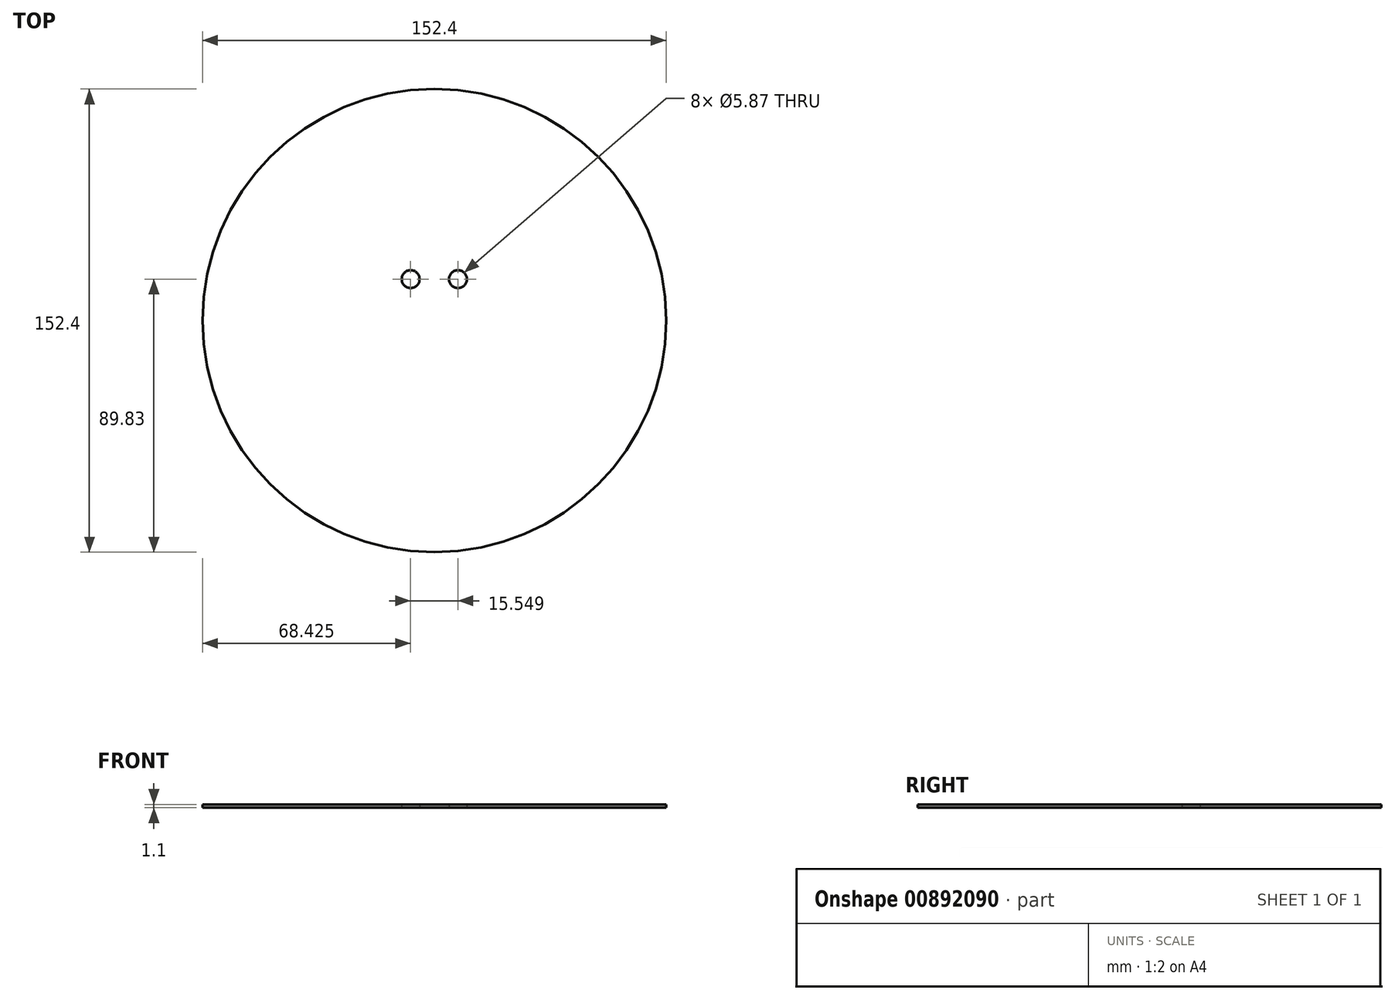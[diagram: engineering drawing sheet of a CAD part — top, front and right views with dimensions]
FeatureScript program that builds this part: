
annotation { "Feature Type Name" : "Feature", "Feature Type Description" : "" }
export const myFeature = defineFeature(function(context is Context, id is Id, definition is map)
    precondition{}
    {
        {
            var Q0;
            Q0=qCreatedBy(makeId("Top.planeOp"),FACE);
            var sketch = newSketch(context, id + "F0", { "sketchPlane" : qUnion([Q0])});
            skCircle(sketch, "E0", {"center": v(0, 0) * mm, "radius": 76.2 * mm});
            skFitSpline(sketch, "E1", {"points": [v(-19.87, 16.28) * mm, v(-18.8, 22.53) * mm, v(-13.5, 25.19) * mm, v(-5.12, 27.18) * mm, v(0, 27.18) * mm], "startDerivative": vector(0.03, 28.86) * mm, "endDerivative": vector(21.37, -1.59) * mm});
            skPoint(sketch, "E2.1.internal.orphan", {"position": v(-19.87, 4.85) * mm});
            skPoint(sketch, "E2.2.internal.orphan", {"position": v(-15.75, 0) * mm});
            skLineSegment(sketch, "E3", {"start": v(-19.87, 15.22) * mm, "end": v(-19.87, 4.85) * mm});
            skLineSegment(sketch, "E4", {"start": v(-19.87, 4.85) * mm, "end": v(-15.75, 0) * mm});
            skLineSegment(sketch, "E5", {"start": v(-15.75, 0) * mm, "end": v(-15.75, -13.62) * mm});
            skLineSegment(sketch, "E6", {"start": v(-15.75, -13.62) * mm, "end": v(-13.22, -13.62) * mm});
            skLineSegment(sketch, "E7", {"start": v(-13.22, -4.32) * mm, "end": v(-12.16, -4.32) * mm});
            skLineSegment(sketch, "E8", {"start": v(-12.16, -13.62) * mm, "end": v(-10.03, -13.62) * mm});
            skLineSegment(sketch, "E9", {"start": v(-8.44, -13.62) * mm, "end": v(-7.5, -13.62) * mm});
            skPoint(sketch, "E10.end.orphan", {"position": v(-10.03, -4.32) * mm});
            skPoint(sketch, "E11.start.orphan", {"position": v(-8.44, -4.32) * mm});
            skPoint(sketch, "E12.end.orphan", {"position": v(-7.5, -4.32) * mm});
            skLineSegment(sketch, "E13", {"start": v(-17.21, -13.62) * mm, "end": v(-10.03, -13.62) * mm});
            skLineSegment(sketch, "E14", {"start": v(-10.03, -4.32) * mm, "end": v(-10.03, -13.62) * mm});
            skLineSegment(sketch, "E15", {"start": v(-10.03, -4.32) * mm, "end": v(-7.5, -4.32) * mm});
            skLineSegment(sketch, "E16", {"start": v(-7.5, -4.32) * mm, "end": v(-7.5, -13.62) * mm});
            skLineSegment(sketch, "E17", {"start": v(-3.65, -13.62) * mm, "end": v(-3.65, -4.32) * mm});
            skLineSegment(sketch, "E18", {"start": v(-7.5, -13.62) * mm, "end": v(-3.65, -13.62) * mm});
            skLineSegment(sketch, "E19", {"start": v(-3.65, -4.32) * mm, "end": v(-1.26, -4.32) * mm});
            skCircle(sketch, "E20", {"center": v(-7.77, 13.63) * mm, "radius": 2.94 * mm});
            skLineSegment(sketch, "E21", {"start": v(-12.7, 22) * mm, "end": v(-3.52, 17.48) * mm});
            skFitSpline(sketch, "E22.MirrorCS", {"points": [v(19.87, 16.28) * mm, v(18.8, 22.53) * mm, v(13.5, 25.19) * mm, v(5.12, 27.18) * mm, v(0, 27.18) * mm], "startDerivative": vector(-0.03, 28.86) * mm, "endDerivative": vector(-21.37, -1.59) * mm});
            skLineSegment(sketch, "E23.MirrorCS", {"start": v(12.7, 22) * mm, "end": v(3.52, 17.48) * mm});
            skCircle(sketch, "E24.MirrorC", {"center": v(7.77, 13.63) * mm, "radius": 2.94 * mm});
            skLineSegment(sketch, "E25.MirrorCS", {"start": v(3.65, -13.62) * mm, "end": v(3.65, -4.32) * mm});
            skLineSegment(sketch, "E26.MirrorCS", {"start": v(7.5, -13.62) * mm, "end": v(3.65, -13.62) * mm});
            skLineSegment(sketch, "E27.MirrorCS", {"start": v(3.65, -4.32) * mm, "end": v(1.26, -4.32) * mm});
            skLineSegment(sketch, "E28.MirrorCS", {"start": v(10.03, -4.32) * mm, "end": v(10.03, -13.62) * mm});
            skPoint(sketch, "E29.MirrorP", {"position": v(8.44, -4.32) * mm});
            skLineSegment(sketch, "E30.MirrorCS", {"start": v(7.5, -4.32) * mm, "end": v(7.5, -13.62) * mm});
            skLineSegment(sketch, "E31.MirrorCS", {"start": v(17.21, -13.62) * mm, "end": v(10.03, -13.62) * mm});
            skLineSegment(sketch, "E32.MirrorCS", {"start": v(15.75, 0) * mm, "end": v(15.75, -13.62) * mm});
            skLineSegment(sketch, "E33.MirrorCS", {"start": v(19.87, 4.85) * mm, "end": v(15.75, 0) * mm});
            skLineSegment(sketch, "E34.MirrorCS", {"start": v(19.87, 15.22) * mm, "end": v(19.87, 4.85) * mm});
            skSolve(sketch);
        }
        {
            var Q0;
            Q0 = qSketchRegion(id + "F0", true);
            extrude(context, id + "F1", {"entities" : qUnion([Q0]), "depth" : 1.1 * mm, "offsetDistance" : 25.4 * mm});
        }
    });
